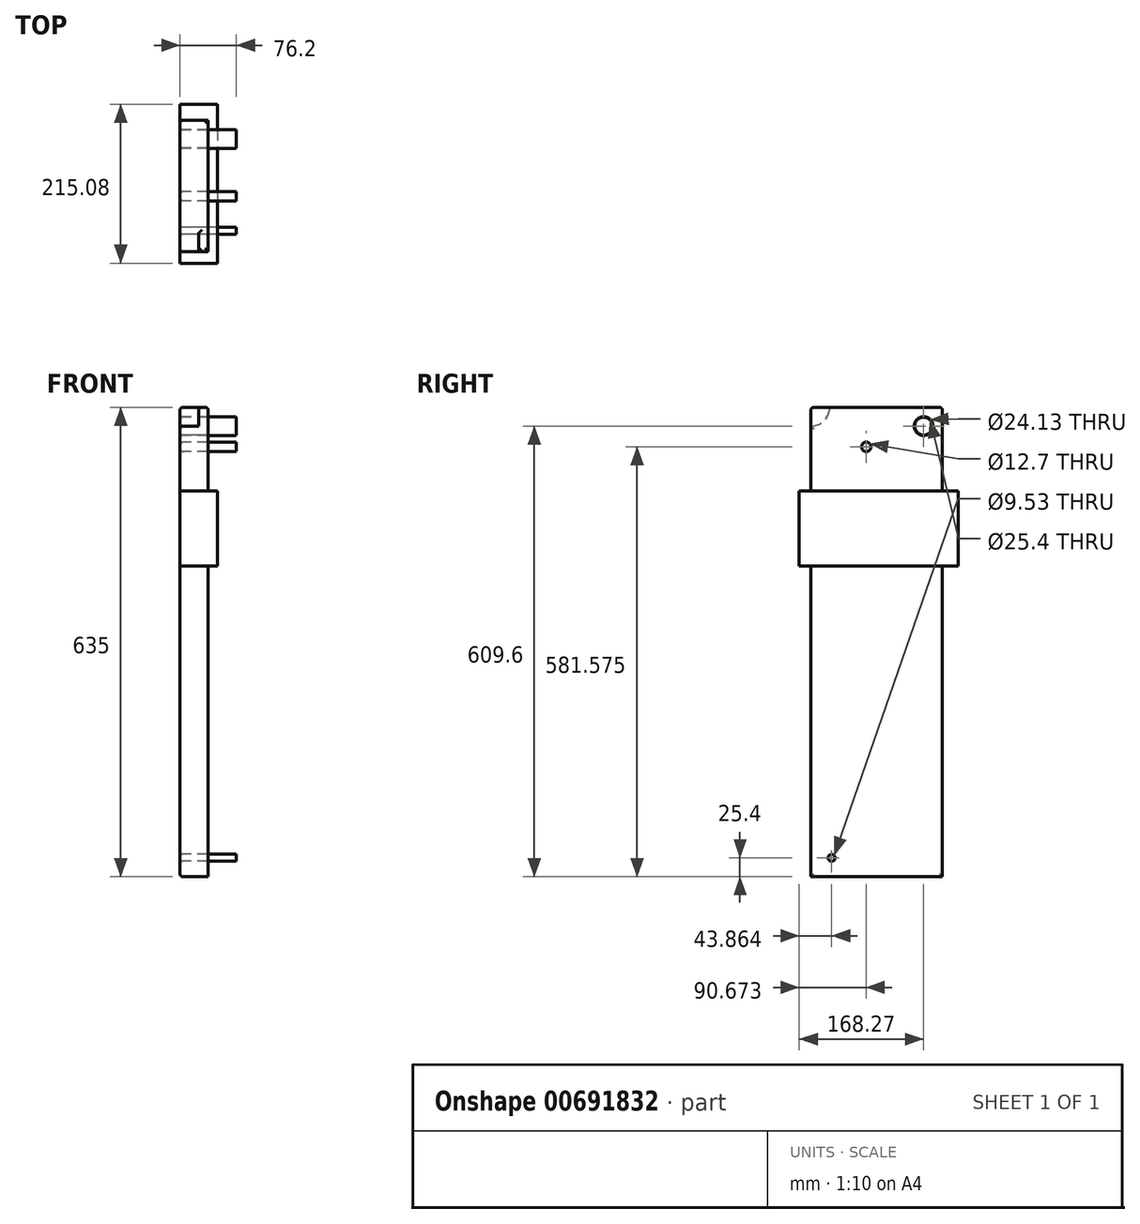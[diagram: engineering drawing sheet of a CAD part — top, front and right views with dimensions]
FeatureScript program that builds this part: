
annotation { "Feature Type Name" : "Feature", "Feature Type Description" : "" }
export const myFeature = defineFeature(function(context is Context, id is Id, definition is map)
    precondition{}
    {
        {
            var Q0;
            Q0=qCreatedBy(makeId("Front.planeOp"),FACE);
            var sketch = newSketch(context, id + "F0", { "sketchPlane" : qUnion([Q0])});
            skLineSegment(sketch, "E0.bottom", {"start": v(0, 0) * mm, "end": v(38.1, 0) * mm});
            skLineSegment(sketch, "E0.top", {"start": v(0, -635) * mm, "end": v(38.1, -635) * mm});
            skLineSegment(sketch, "E0.left", {"start": v(0, 0) * mm, "end": v(0, -635) * mm});
            skLineSegment(sketch, "E0.right", {"start": v(38.1, 0) * mm, "end": v(38.1, -635) * mm});
            skSolve(sketch);
        }
        {
            var Q0;
            Q0 = qSketchRegion(id + "F0", true);
            extrude(context, id + "F1", {"entities" : qUnion([Q0]), "oppositeDirection" : true, "depth" : 177.8 * mm, "offsetDistance" : 25.4 * mm});
        }
        {
            var Q0;
            Q0=qCreatedBy(makeId("Right.planeOp"),FACE);
            var sketch = newSketch(context, id + "F2", { "sketchPlane" : qUnion([Q0])});
            skCircle(sketch, "E1", {"center": v(0, 0) * mm, "radius": 25.4 * mm});
            skCircle(sketch, "E2", {"center": v(152.4, -25.4) * mm, "radius": 12.7 * mm});
            skCircle(sketch, "E3", {"center": v(74.8, -53.42) * mm, "radius": 6.35 * mm});
            skCircle(sketch, "E4", {"center": v(28, -609.6) * mm, "radius": 4.76 * mm});
            skCircle(sketch, "E5", {"center": v(152.4, -25.4) * mm, "radius": 12.07 * mm});
            skSolve(sketch);
        }
        {
            var Q0;
            Q0 = qSketchRegion(id + "F2", true);
            extrude(context, id + "F3", {"entities" : qUnion([Q0]), "operationType" : NewBodyOperationType.REMOVE, "depth" : 25.4 * mm, "offsetDistance" : 25.4 * mm});
        }
        {
            var Q0;
            Q0=makeQuery(id+"F3.boolean.opBoolean","COPY",FACE,{"derivedFrom":makeQuery(id+"F3.opExtrude","CAP_FACE",FACE,{"disambiguationData":[OSD([sQuery(id+"F2.wireOp",EDGE,"E3")])],"isStart":false})});
            extrude(context, id + "F4", {"entities" : qUnion([Q0]), "operationType" : NewBodyOperationType.REMOVE, "endBound" : BoundingType.THROUGH_ALL, "oppositeDirection" : true, "depth" : 25.4 * mm, "offsetDistance" : 25.4 * mm});
        }
        {
            var Q0;
            Q0=makeQuery(id+"F3.boolean.opBoolean","COPY",FACE,{"derivedFrom":makeQuery(id+"F3.opExtrude","CAP_FACE",FACE,{"disambiguationData":[OSD([sQuery(id+"F2.wireOp",EDGE,"E2")])],"isStart":false})});
            extrude(context, id + "F5", {"entities" : qUnion([Q0]), "operationType" : NewBodyOperationType.REMOVE, "endBound" : BoundingType.THROUGH_ALL, "oppositeDirection" : true, "depth" : 25.4 * mm, "offsetDistance" : 25.4 * mm});
        }
        {
            var Q0;
            Q0=makeQuery(id+"F3.boolean.opBoolean","COPY",FACE,{"derivedFrom":makeQuery(id+"F3.opExtrude","CAP_FACE",FACE,{"disambiguationData":[OSD([sQuery(id+"F2.wireOp",EDGE,"E4")])],"isStart":false})});
            extrude(context, id + "F6", {"entities" : qUnion([Q0]), "operationType" : NewBodyOperationType.REMOVE, "endBound" : BoundingType.THROUGH_ALL, "oppositeDirection" : true, "depth" : 25.4 * mm, "offsetDistance" : 25.4 * mm});
        }
        {
            var Q0;
            Q0=makeQuery(id+"F1.opExtrude","SWEPT_FACE",FACE,{"disambiguationData":[OSD([sQuery(id+"F0.wireOp",EDGE,"E0.left")])]});
            fillet(context, id + "F7", {"entities" : qUnion([Q0]), "radius" : 3.8 * mm, "tangentPropagation" : true, "allowEdgeOverflow" : false});
        }
        {
            var Q0;
            Q0=makeQuery(id+"F1.opExtrude","SWEPT_FACE",FACE,{"disambiguationData":[OSD([sQuery(id+"F0.wireOp",EDGE,"E0.bottom")])]});
            fillet(context, id + "F8", {"entities" : qUnion([Q0]), "radius" : 3.8 * mm, "tangentPropagation" : true, "allowEdgeOverflow" : false});
        }
        {
            var Q0;
            Q0 = qSketchRegion(id + "F2", true);
            extrude(context, id + "F9", {"entities" : qUnion([Q0]), "depth" : 76.2 * mm, "offsetDistance" : 25.4 * mm});
        }
        {
            var Q0;
            Q0=makeQuery(id+"F9.opExtrude","SWEPT_FACE",FACE,{"disambiguationData":[OSD([sQuery(id+"F2.wireOp",EDGE,"E2")])]});
            var Q1;
            Q1=makeQuery(id+"F3.boolean.opBoolean","SPLIT",FACE,{"disambiguationData":[TD([makeQuery(id+"F3.opExtrude","SWEPT_FACE",FACE,{"disambiguationData":[OSD([sQuery(id+"F2.wireOp",EDGE,"E5")])]})])],"derivedFrom":makeQuery(id+"F1.opExtrude","SWEPT_FACE",FACE,{"disambiguationData":[OSD([sQuery(id+"F0.wireOp",EDGE,"E0.left")])]})});
            fillet(context, id + "F10", {"entities" : qUnion([Q0, Q1]), "radius" : 5.08 * mm, "tangentPropagation" : true, "allowEdgeOverflow" : false});
        }
        {
            var Q0;
            Q0=makeQuery(id+"F9.opExtrude","CAP_FACE",FACE,{"disambiguationData":[OSD([sQuery(id+"F2.wireOp",EDGE,"E3")])],"isStart":true});
            fillet(context, id + "F11", {"entities" : qUnion([Q0]), "radius" : 5.08 * mm, "tangentPropagation" : true, "allowEdgeOverflow" : false});
        }
        {
            var Q0;
            Q0=makeQuery(id+"F9.opExtrude","SWEPT_BODY",BODY,{"disambiguationData":[OSD([sQuery(id+"F2.wireOp",EDGE,"E1")])]});
            deleteBodies(context, id + "F12", {"entities" : qUnion([Q0])});
        }
        {
            var Q0;
            Q0=makeQuery(id+"F9.opExtrude","CAP_FACE",FACE,{"disambiguationData":[OSD([sQuery(id+"F2.wireOp",EDGE,"E4")])],"isStart":true});
            fillet(context, id + "F13", {"entities" : qUnion([Q0]), "radius" : 1.27 * mm, "tangentPropagation" : true, "allowEdgeOverflow" : false});
        }
        {
            var Q0;
            Q0=qCreatedBy(makeId("Right.planeOp"),FACE);
            var sketch = newSketch(context, id + "F14", { "sketchPlane" : qUnion([Q0])});
            skLineSegment(sketch, "E6.bottom", {"start": v(199.2, -112.93) * mm, "end": v(-15.87, -112.93) * mm});
            skLineSegment(sketch, "E6.top", {"start": v(199.2, -214.45) * mm, "end": v(-15.87, -214.45) * mm});
            skLineSegment(sketch, "E6.left", {"start": v(199.2, -112.93) * mm, "end": v(199.2, -214.45) * mm});
            skLineSegment(sketch, "E6.right", {"start": v(-15.87, -112.93) * mm, "end": v(-15.87, -214.45) * mm});
            skSolve(sketch);
        }
        {
            var Q0;
            Q0=makeQuery(id+"F14.imprint","IMPRINT",FACE,{"disambiguationData":[TD([[makeQuery(id+"F14.imprint","IMPRINT",EDGE,{"derivedFrom":sQuery(id+"F14.wireOp",EDGE,"E6.bottom")}),1.0]])]});
            extrude(context, id + "F15", {"entities" : qUnion([Q0]), "operationType" : NewBodyOperationType.ADD, "depth" : 50.8 * mm, "offsetDistance" : 25.4 * mm});
        }
    });
